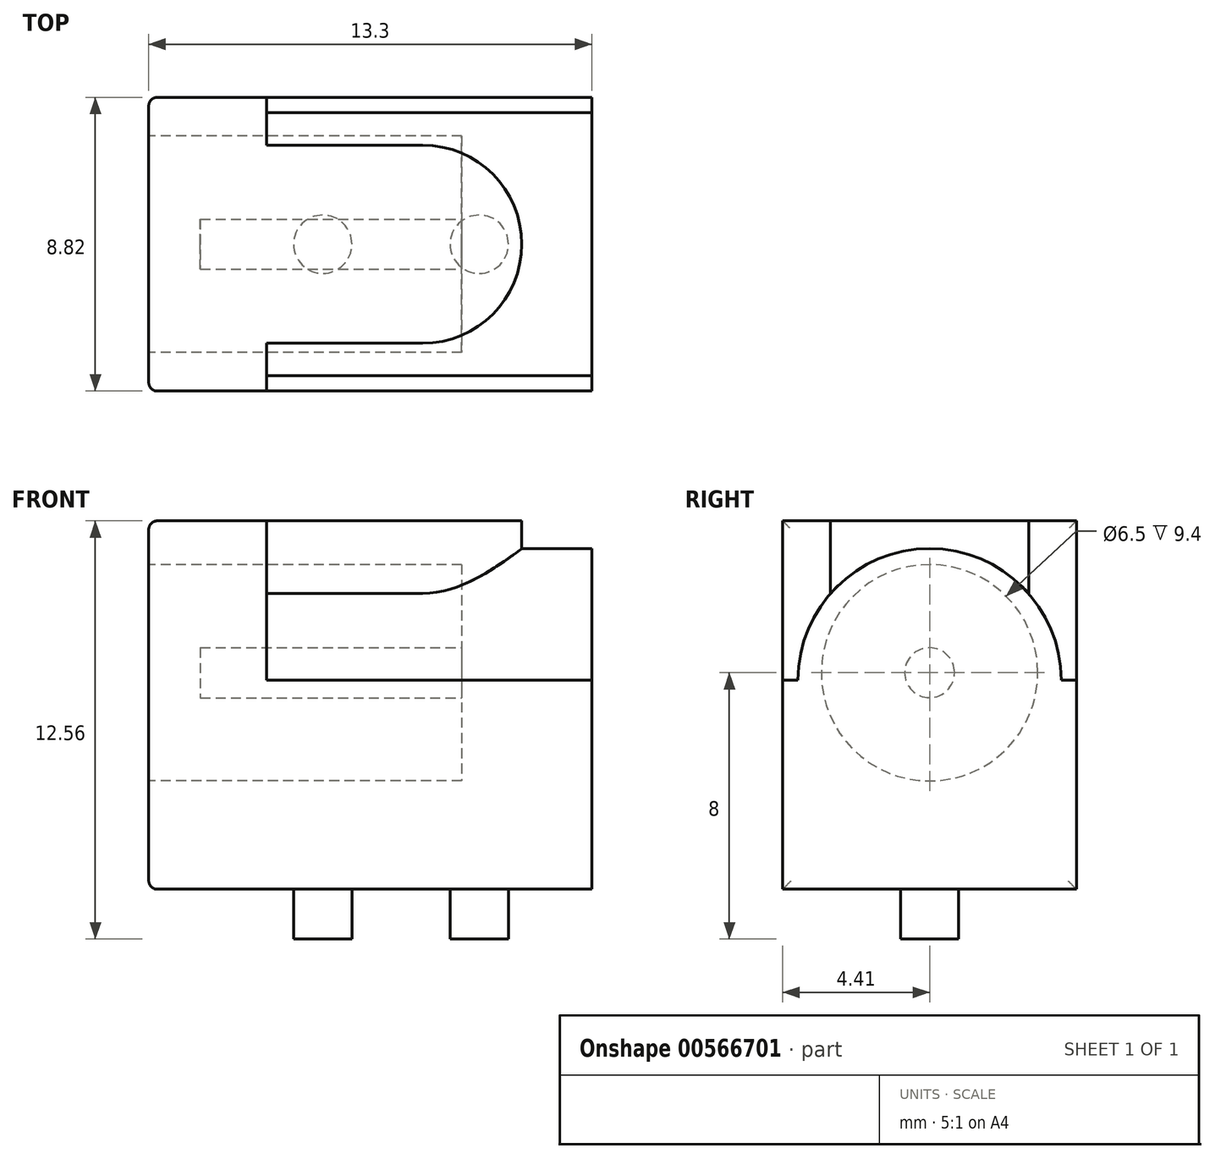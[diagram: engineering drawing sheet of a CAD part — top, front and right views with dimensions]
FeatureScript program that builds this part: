
annotation { "Feature Type Name" : "Feature", "Feature Type Description" : "" }
export const myFeature = defineFeature(function(context is Context, id is Id, definition is map)
    precondition{}
    {
        {
            var Q0;
            Q0=qCreatedBy(makeId("Top.planeOp"),FACE);
            var sketch = newSketch(context, id + "F0", { "sketchPlane" : qUnion([Q0])});
            skLineSegment(sketch, "E0.bottom", {"start": v(6.65, 4.41) * mm, "end": v(-6.65, 4.41) * mm});
            skLineSegment(sketch, "E0.top", {"start": v(6.65, -4.4) * mm, "end": v(-6.65, -4.4) * mm});
            skLineSegment(sketch, "E0.left", {"start": v(6.65, 4.41) * mm, "end": v(6.65, -4.4) * mm});
            skLineSegment(sketch, "E0.right", {"start": v(-6.65, 4.41) * mm, "end": v(-6.65, -4.4) * mm});
            skPoint(sketch, "E0.middle", {"position": v(0, 0) * mm});
            skSolve(sketch);
        }
        {
            var Q0;
            Q0=makeQuery(id+"F0.imprint","IMPRINT",FACE,{"disambiguationData":[TD([[makeQuery(id+"F0.imprint","IMPRINT",EDGE,{"derivedFrom":sQuery(id+"F0.wireOp",EDGE,"E0.bottom")}),1.0]])]});
            extrude(context, id + "F1", {"entities" : qUnion([Q0]), "depth" : 6.28 * mm, "offsetDistance" : 25 * mm});
        }
        {
            var Q0;
            Q0=makeQuery(id+"F1.opExtrude","SWEPT_FACE",FACE,{"disambiguationData":[OSD([sQuery(id+"F0.wireOp",EDGE,"E0.left")])]});
            var sketch = newSketch(context, id + "F2", { "sketchPlane" : qUnion([Q0])});
            skCircle(sketch, "E1", {"center": v(0, 6.28) * mm, "radius": 3.95 * mm});
            skSolve(sketch);
        }
        {
            var Q0;
            Q0 = qSketchRegion(id + "F2", true);
            var Q1;
            Q1=makeQuery(id+"F1.opExtrude","SWEPT_FACE",FACE,{"disambiguationData":[OSD([sQuery(id+"F0.wireOp",EDGE,"E0.right")])]});
            extrude(context, id + "F3", {"entities" : qUnion([Q0]), "operationType" : NewBodyOperationType.ADD, "endBound" : BoundingType.UP_TO_SURFACE, "oppositeDirection" : true, "depth" : 25 * mm, "endBoundEntityFace" : qUnion([Q1]), "offsetDistance" : 25 * mm});
        }
        {
            var Q0;
            {var subQ0=sQuery(id+"F0.wireOp",EDGE,"E0.right");Q0=makeQuery(id+"F3.boolean.opBoolean","MERGE",FACE,{"derivedFrom":[makeQuery(id+"F1.opExtrude","SWEPT_FACE",FACE,{"disambiguationData":[OSD([subQ0])]}),makeQuery(id+"F3.opExtrude","CAP_FACE",FACE,{"disambiguationData":[OSD([subQ0])],"isStart":false})]});}
            var sketch = newSketch(context, id + "F4", { "sketchPlane" : qUnion([Q0])});
            skLineSegment(sketch, "E2.bottom", {"start": v(-4.41, 0) * mm, "end": v(4.4, 0) * mm});
            skLineSegment(sketch, "E2.top", {"start": v(-4.41, 11.06) * mm, "end": v(4.4, 11.06) * mm});
            skLineSegment(sketch, "E2.left", {"start": v(-4.41, 0) * mm, "end": v(-4.41, 11.06) * mm});
            skLineSegment(sketch, "E2.right", {"start": v(4.4, 0) * mm, "end": v(4.4, 11.06) * mm});
            skSolve(sketch);
        }
        {
            var Q0;
            Q0 = qSketchRegion(id + "F4", true);
            extrude(context, id + "F5", {"entities" : qUnion([Q0]), "operationType" : NewBodyOperationType.ADD, "oppositeDirection" : true, "depth" : 3.54 * mm, "offsetDistance" : 25 * mm});
        }
        {
            var Q0;
            Q0=makeQuery(id+"F5.opExtrude","CAP_EDGE",EDGE,{"disambiguationData":[OSD([sQuery(id+"F4.wireOp",EDGE,"E2.top")])],"isStart":true});
            var Q1;
            Q1=makeQuery(id+"F5.boolean.opBoolean","MERGE",EDGE,{"derivedFrom":[makeQuery(id+"F1.opExtrude","SWEPT_EDGE",EDGE,{"disambiguationData":[OSD([sQuery(id+"F0.wireOp",EDGE,"E0.bottom"),sQuery(id+"F0.wireOp",EDGE,"E0.right")])]}),makeQuery(id+"F5.opExtrude","CAP_EDGE",EDGE,{"disambiguationData":[OSD([sQuery(id+"F4.wireOp",EDGE,"E2.left")])],"isStart":true})]});
            var Q2;
            Q2=makeQuery(id+"F1.opExtrude","CAP_EDGE",EDGE,{"disambiguationData":[OSD([sQuery(id+"F0.wireOp",EDGE,"E0.right")])],"isStart":true});
            var Q3;
            Q3=makeQuery(id+"F5.boolean.opBoolean","MERGE",EDGE,{"derivedFrom":[makeQuery(id+"F1.opExtrude","SWEPT_EDGE",EDGE,{"disambiguationData":[OSD([sQuery(id+"F0.wireOp",EDGE,"E0.top"),sQuery(id+"F0.wireOp",EDGE,"E0.right")])]}),makeQuery(id+"F5.opExtrude","CAP_EDGE",EDGE,{"disambiguationData":[OSD([sQuery(id+"F4.wireOp",EDGE,"E2.right")])],"isStart":true})]});
            fillet(context, id + "F6", {"entities" : qUnion([Q0, Q1, Q2, Q3]), "radius" : .25 * mm, "tangentPropagation" : true, "allowEdgeOverflow" : false});
        }
        {
            var Q0;
            Q0=makeQuery(id+"F5.opExtrude","SWEPT_FACE",FACE,{"disambiguationData":[OSD([sQuery(id+"F4.wireOp",EDGE,"E2.top")])]});
            var sketch = newSketch(context, id + "F7", { "sketchPlane" : qUnion([Q0])});
            skLineSegment(sketch, "E3.bottom", {"start": v(-3.11, -2.97) * mm, "end": v(1.57, -2.98) * mm});
            skLineSegment(sketch, "E3.top", {"start": v(-3.11, 2.97) * mm, "end": v(1.57, 2.97) * mm});
            skLineSegment(sketch, "E3.left", {"start": v(-3.11, -2.97) * mm, "end": v(-3.11, 2.97) * mm});
            skLineSegment(sketch, "E3.right", {"start": v(1.57, -2.98) * mm, "end": v(1.57, 2.98) * mm});
            skArc(sketch, "E4", {"start": v(1.57, -2.98) * mm, "mid": v(4.55, 0) * mm, "end": v(1.57, 2.98) * mm});
            skPoint(sketch, "E5", {"position": v(4.55, 0) * mm});
            skSolve(sketch);
        }
        {
            var Q0;
            Q0 = qSketchRegion(id + "F7", true);
            extrude(context, id + "F8", {"entities" : qUnion([Q0]), "operationType" : NewBodyOperationType.ADD, "endBound" : BoundingType.UP_TO_NEXT, "oppositeDirection" : true, "depth" : 25 * mm, "offsetDistance" : 25 * mm});
        }
        {
            var Q0;
            {var subQ0=sQuery(id+"F0.wireOp",EDGE,"E0.right");Q0=makeQuery(id+"F5.boolean.opBoolean","MERGE",FACE,{"derivedFrom":[makeQuery(id+"F3.boolean.opBoolean","MERGE",FACE,{"derivedFrom":[makeQuery(id+"F1.opExtrude","SWEPT_FACE",FACE,{"disambiguationData":[OSD([subQ0])]}),makeQuery(id+"F3.opExtrude","CAP_FACE",FACE,{"disambiguationData":[OSD([subQ0])],"isStart":false})]}),makeQuery(id+"F5.opExtrude","CAP_FACE",FACE,{"disambiguationData":[OSD([sQuery(id+"F4.wireOp",EDGE,"E2.bottom"),sQuery(id+"F4.wireOp",EDGE,"E2.top"),sQuery(id+"F4.wireOp",EDGE,"E2.left"),sQuery(id+"F4.wireOp",EDGE,"E2.right")])],"isStart":true})]});}
            var sketch = newSketch(context, id + "F9", { "sketchPlane" : qUnion([Q0])});
            skCircle(sketch, "E6", {"center": v(0, 6.5) * mm, "radius": 3.25 * mm});
            skSolve(sketch);
        }
        {
            var Q0;
            Q0 = qSketchRegion(id + "F9", true);
            extrude(context, id + "F10", {"entities" : qUnion([Q0]), "operationType" : NewBodyOperationType.REMOVE, "oppositeDirection" : true, "depth" : 9.4 * mm, "offsetDistance" : 25 * mm});
        }
        {
            var Q0;
            Q0=makeQuery(id+"F10.boolean.opBoolean","COPY",FACE,{"derivedFrom":makeQuery(id+"F10.opExtrude","CAP_FACE",FACE,{"disambiguationData":[OSD([sQuery(id+"F9.wireOp",EDGE,"E6")])],"isStart":false})});
            var sketch = newSketch(context, id + "F11", { "sketchPlane" : qUnion([Q0])});
            skCircle(sketch, "E7", {"center": v(0, 6.5) * mm, "radius": 0.75 * mm});
            skSolve(sketch);
        }
        {
            var Q0;
            Q0 = qSketchRegion(id + "F11", true);
            extrude(context, id + "F12", {"entities" : qUnion([Q0]), "operationType" : NewBodyOperationType.ADD, "depth" : 7.85 * mm, "offsetDistance" : 25 * mm});
        }
        {
            var Q0;
            Q0=makeQuery(id+"F1.opExtrude","CAP_FACE",FACE,{"disambiguationData":[OSD([sQuery(id+"F0.wireOp",EDGE,"E0.bottom"),sQuery(id+"F0.wireOp",EDGE,"E0.top"),sQuery(id+"F0.wireOp",EDGE,"E0.left"),sQuery(id+"F0.wireOp",EDGE,"E0.right")])],"isStart":true});
            var sketch = newSketch(context, id + "F13", { "sketchPlane" : qUnion([Q0])});
            skCircle(sketch, "E8", {"center": v(-1.43, 0) * mm, "radius": 0.88 * mm});
            skCircle(sketch, "E9", {"center": v(3.27, 0) * mm, "radius": 0.88 * mm});
            skSolve(sketch);
        }
        {
            var Q0;
            Q0=makeQuery(id+"F13.imprint","IMPRINT",FACE,{"disambiguationData":[TD([[makeQuery(id+"F13.imprint","IMPRINT",EDGE,{"derivedFrom":sQuery(id+"F13.wireOp",EDGE,"E8")}),1.0]])]});
            var Q1;
            Q1=makeQuery(id+"F13.imprint","IMPRINT",FACE,{"disambiguationData":[TD([[makeQuery(id+"F13.imprint","IMPRINT",EDGE,{"derivedFrom":sQuery(id+"F13.wireOp",EDGE,"E9")}),1.0]])]});
            extrude(context, id + "F14", {"entities" : qUnion([Q0, Q1]), "operationType" : NewBodyOperationType.ADD, "depth" : 1.5 * mm, "offsetDistance" : 25 * mm});
        }
        {
            var Q0;
            Q0=makeQuery(id+"F12.opExtrude","CAP_FACE",FACE,{"disambiguationData":[OSD([sQuery(id+"F11.wireOp",EDGE,"E7")])],"isStart":false});
            var sketch = newSketch(context, id + "F15", { "sketchPlane" : qUnion([Q0])});
            skCircle(sketch, "E10.0", {"center": v(0, 6.5) * mm, "radius": 0.75 * mm});
            skLineSegment(sketch, "E11", {"start": v(-0.75, 6.5) * mm, "end": v(0.75, 6.5) * mm});
            skSolve(sketch);
        }
        {
            var Q0;
            Q0=sQuery(id+"F15.wireOp",EDGE,"E11");
            cPlane(context, id + "F16", {"entities" : qUnion([Q0]), "cplaneType" : CPlaneType.LINE_ANGLE, "offset" : 25 * mm, "angle" : 0 * degree, "width" : 150 * mm, "height" : 150 * mm});
        }
    });
